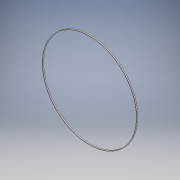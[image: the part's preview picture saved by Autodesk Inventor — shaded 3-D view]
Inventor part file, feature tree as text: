
AUTODESK INVENTOR PART (.ipt)
format: ipt  version: 2019 (Build 230136000, 136)  size: 105,472 bytes
history: native  units: mm
features: extrude x2, sketch x2
ambient origin geometry x8: Origin, YZ Plane, XZ Plane, XY Plane, X Axis, Y Axis, Z Axis, Center Point
bodies: Solid1 (feature_tree)
feature tree (4):
  extrude  "Extrusion1"  Depth=5.0mm TaperAngle=0.0deg
  extrude  "Extrusion2"  Depth=0.27mm TaperAngle=0.0deg
  sketch  "Sketch1"  dims[d0=423.0mm d1=5.0mm d2=0.0mm]
  sketch  "Sketch2"  dims[d3=419.0mm d4=0.27mm d5=0.0mm]
